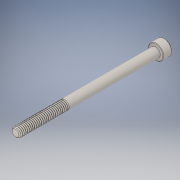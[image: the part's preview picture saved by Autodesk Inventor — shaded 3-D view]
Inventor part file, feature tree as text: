
AUTODESK INVENTOR PART (.ipt)
format: ipt  version: 2017 (Build 210142000, 142)  size: 696,320 bytes
history: native  units: in
note: dims shown in document units (in); Inventor stores cm internally (conversion verified against a paired STEP export)
features: chamfer x1
ambient origin geometry x8: Origin, YZ Plane, XZ Plane, XY Plane, X Axis, Y Axis, Z Axis, Center Point
bodies: Solid1 (feature_tree)
feature tree (1):
  chamfer  "Chamfer2"  [1 undecoded]
note: 1 required parameter value undecoded (feature->parameter linkage not recoverable at this tier; creation-order binding heuristic only, values carry confidence <= 0.55)
